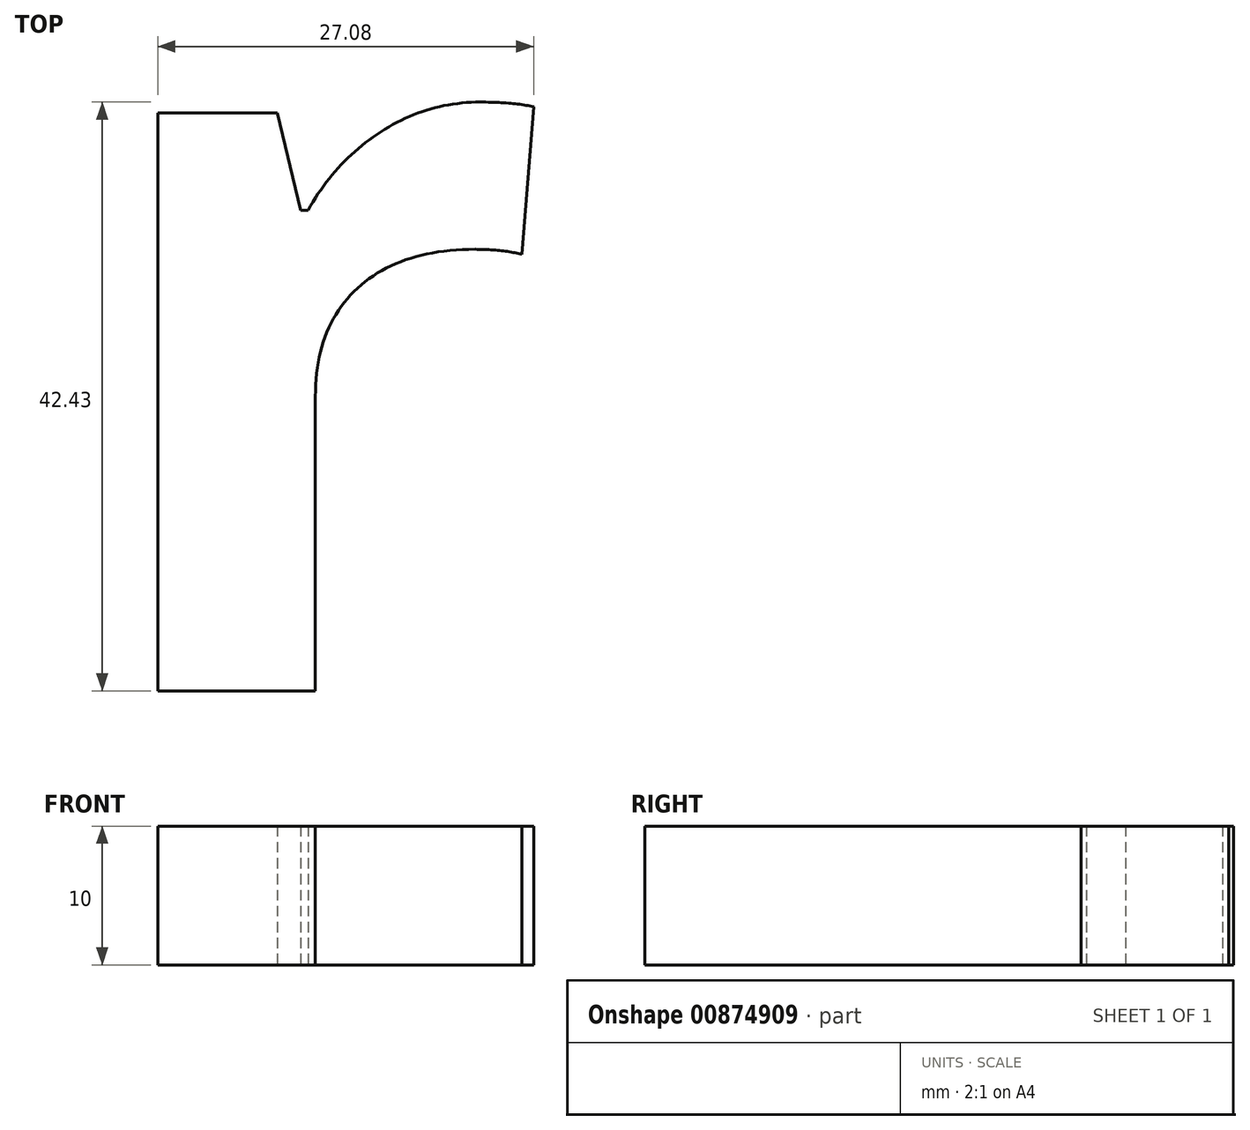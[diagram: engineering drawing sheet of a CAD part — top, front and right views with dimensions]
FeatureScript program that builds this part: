
annotation { "Feature Type Name" : "Feature", "Feature Type Description" : "" }
export const myFeature = defineFeature(function(context is Context, id is Id, definition is map)
    precondition{}
    {
        {
            var Q0;
            Q0=qCreatedBy(makeId("Top.planeOp"),FACE);
            var sketch = newSketch(context, id + "F0", { "sketchPlane" : qUnion([Q0])});
            skText(sketch, "E0", { "text": "r", "fontName": "OpenSans-Bold.ttf"});
            const initialGuessF0  = {"E0": [0, 0, 1, 0, 0.05493]};
            skSetInitialGuess(sketch, initialGuessF0);
            skSolve(sketch);
        }
        {
            var Q0;
            Q0=makeQuery(id+"F0.imprint","IMPRINT",FACE,{"disambiguationData":[TD([[makeQuery(id+"F0.imprint","IMPRINT",EDGE,{"derivedFrom":sQuery(id+"F0.wireOp",EDGE,"E0.sketch_text.stroke-0")}),-1.0]])]});
            extrude(context, id + "F1", {"entities" : qUnion([Q0]), "depth" : 10 * mm, "offsetDistance" : 25 * mm});
        }
    });
